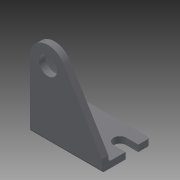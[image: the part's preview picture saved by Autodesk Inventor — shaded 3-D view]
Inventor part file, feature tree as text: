
AUTODESK INVENTOR PART (.ipt)
format: ipt  version: 2014 (Build 180170000, 170)  size: 152,576 bytes
history: native  units: in
note: dims shown in document units (in); Inventor stores cm internally (conversion verified against a paired STEP export)
features: other x14, sketch x8, extrude x5, hole x3
ambient origin geometry x8: Origin, YZ Plane, XZ Plane, XY Plane, X Axis, Y Axis, Z Axis, Center Point
bodies: Solid1 (feature_tree)
feature tree (30):
  extrude  "Extrusion1"  Depth=1.0in TaperAngle=0.0deg
  extrude  "Extrusion2"  Depth=0.1345in TaperAngle=0.0deg
  hole  "Hole1"  [1 undecoded]
  hole  "Hole2"  [1 undecoded]
  hole  "Hole3"  [1 undecoded]
  sketch  "Sketch_6"
  sketch  "Sketch_7"
  extrude  "Extrusion3"  [1 undecoded]
  extrude  "Extrusion4"  [1 undecoded]
  extrude  "Extrusion5"  [1 undecoded]
  other  "to_dummy_R_XY"
  other  "to_dummy_R_YZ"
  other  "to_dummy_R_ZX"
  other  "to_dummy_R_X"
  other  "to_dummy_R_Y"
  other  "to_dummy_R_Z"
  other  "to_dummy_R_Center"
  other  "to_pin_R_XY"
  other  "to_pin_R_YZ"
  other  "to_pin_R_ZX"
  other  "to_pin_R_X"
  other  "to_pin_R_Y"
  other  "to_pin_R_Z"
  other  "to_pin_R_Center"
  sketch  "Sketch_1"  dims[d0=1.5in d1=0.0in d2=1.0in d3=0.0in]
  sketch  "Sketch_2"  dims[d4=0.3775in d5=0.75in d6=0.375in d7=0.25in d8=0.5635in d9=0.1345in d10=0.0in]
  sketch  "Sketch3"  dims[d11=0.266in d12=0.75in d13=0.375in d14=0.25in d15=0.5635in d16=0.1345in d17=0.0in]
  sketch  "Sketch4"  dims[d18=0.266in d19=0.75in d20=0.375in d21=0.25in d22=0.5635in d23=0.1345in d24=0.0in d25=0.1345in d26=0.0in]
  sketch  "Sketch5"  dims[d27=0.1345in d28=0.0in d29=0.1345in d30=0.0in]
  sketch  "Sketch_8"
note: 6 required parameter values undecoded (feature->parameter linkage not recoverable at this tier; creation-order binding heuristic only, values carry confidence <= 0.55)
